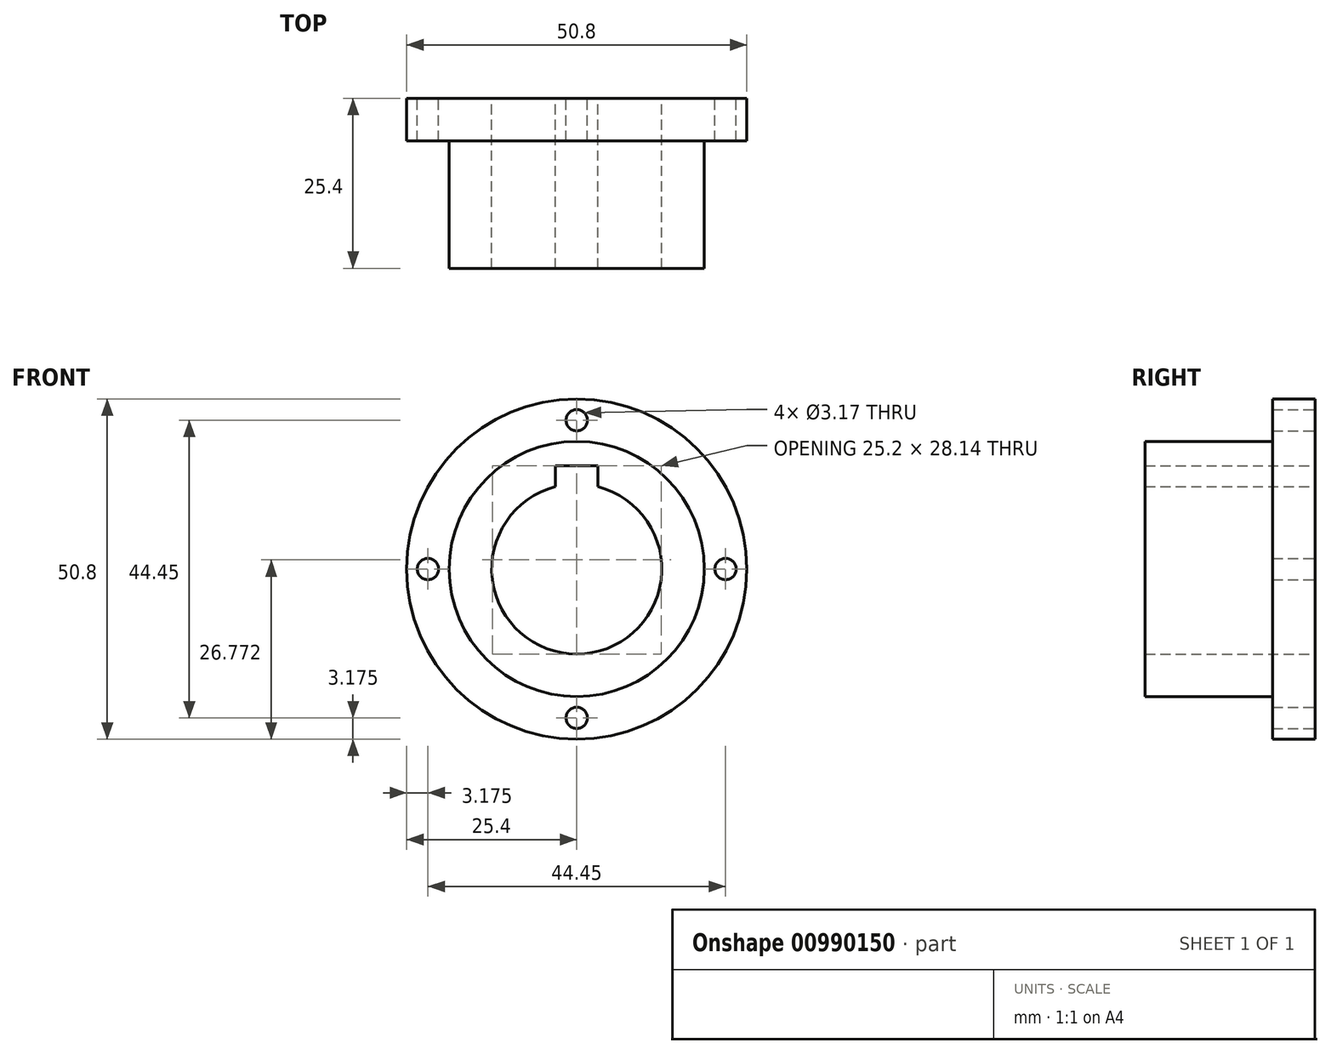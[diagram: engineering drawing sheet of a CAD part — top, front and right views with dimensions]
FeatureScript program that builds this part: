
annotation { "Feature Type Name" : "Feature", "Feature Type Description" : "" }
export const myFeature = defineFeature(function(context is Context, id is Id, definition is map)
    precondition{}
    {
        {
            var Q0;
            Q0=qCreatedBy(makeId("Front.planeOp"),FACE);
            var sketch = newSketch(context, id + "F0", { "sketchPlane" : qUnion([Q0])});
            skCircle(sketch, "E0", {"center": v(0, 0) * mm, "radius": 12.7 * mm});
            skCircle(sketch, "E1", {"center": v(0, 22.23) * mm, "radius": 1.59 * mm});
            skCircle(sketch, "E2", {"center": v(0, 0) * mm, "radius": 22.23 * mm, "construction": true});
            skCircle(sketch, "E3.1.0", {"center": v(-22.23, 0) * mm, "radius": 1.59 * mm});
            skCircle(sketch, "E3.2.0", {"center": v(0, -22.23) * mm, "radius": 1.59 * mm});
            skCircle(sketch, "E3.3.0", {"center": v(22.23, 0) * mm, "radius": 1.59 * mm});
            skCircle(sketch, "E4", {"center": v(0, 0) * mm, "radius": 25.4 * mm});
            skSolve(sketch);
        }
        {
            var Q0;
            Q0 = qSketchRegion(id + "F0", true);
            extrude(context, id + "F1", {"entities" : qUnion([Q0]), "depth" : 6.35 * mm, "offsetDistance" : 25.4 * mm});
        }
        {
            var Q0;
            Q0=qCreatedBy(makeId("Front.planeOp"),FACE);
            var sketch = newSketch(context, id + "F2", { "sketchPlane" : qUnion([Q0])});
            skCircle(sketch, "E5", {"center": v(0, 0) * mm, "radius": 19.05 * mm});
            skCircle(sketch, "E6.0", {"center": v(0, 0) * mm, "radius": 12.7 * mm});
            skSolve(sketch);
        }
        {
            var Q0;
            Q0=makeQuery(id+"F2.imprint","IMPRINT",FACE,{"disambiguationData":[TD([[makeQuery(id+"F2.imprint","IMPRINT",EDGE,{"derivedFrom":sQuery(id+"F2.wireOp",EDGE,"E5")}),1.0]])]});
            extrude(context, id + "F3", {"entities" : qUnion([Q0]), "operationType" : NewBodyOperationType.ADD, "depth" : 25.4 * mm, "offsetDistance" : 25.4 * mm});
        }
        {
            var Q0;
            Q0=qCreatedBy(makeId("Front.planeOp"),FACE);
            var sketch = newSketch(context, id + "F4", { "sketchPlane" : qUnion([Q0])});
            skLineSegment(sketch, "E7.bottom", {"start": v(-3.18, 0) * mm, "end": v(3.18, 0) * mm});
            skLineSegment(sketch, "E7.top", {"start": v(-3.18, 15.44) * mm, "end": v(3.17, 15.44) * mm});
            skLineSegment(sketch, "E7.left", {"start": v(-3.18, 0) * mm, "end": v(-3.17, 15.44) * mm});
            skLineSegment(sketch, "E7.right", {"start": v(3.17, 0) * mm, "end": v(3.18, 15.44) * mm});
            skPoint(sketch, "E8", {"position": v(0, 12.7) * mm});
            skLineSegment(sketch, "E9", {"start": v(0, 12.7) * mm, "end": v(0, 15.44) * mm, "construction": true});
            skSolve(sketch);
        }
        {
            var Q0;
            Q0=makeQuery(id+"F4.imprint","IMPRINT",FACE,{"disambiguationData":[TD([[makeQuery(id+"F4.imprint","IMPRINT",EDGE,{"derivedFrom":sQuery(id+"F4.wireOp",EDGE,"E7.bottom")}),1.0]])]});
            extrude(context, id + "F5", {"entities" : qUnion([Q0]), "operationType" : NewBodyOperationType.REMOVE, "endBound" : BoundingType.THROUGH_ALL, "depth" : 25.4 * mm, "offsetDistance" : 25.4 * mm});
        }
    });
